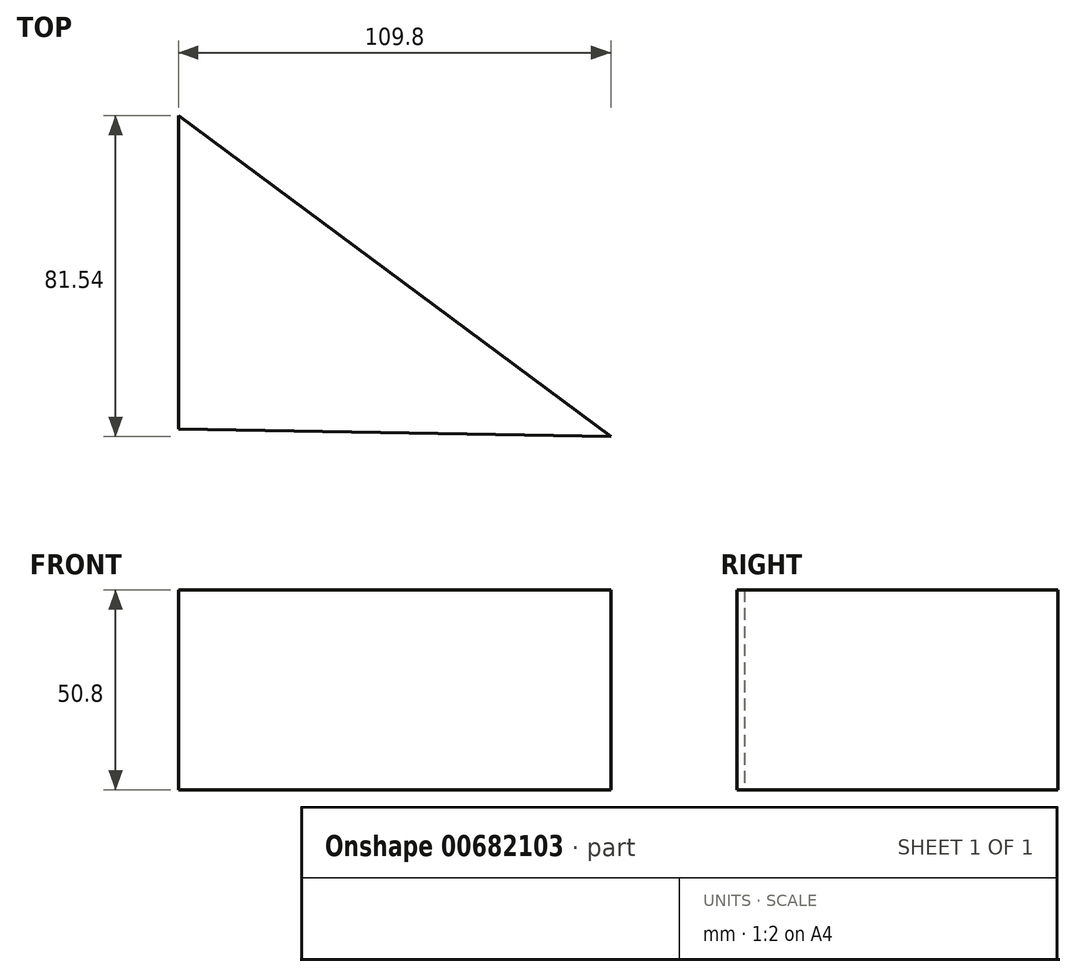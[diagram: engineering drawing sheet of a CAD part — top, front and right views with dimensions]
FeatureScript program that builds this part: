
annotation { "Feature Type Name" : "Feature", "Feature Type Description" : "" }
export const myFeature = defineFeature(function(context is Context, id is Id, definition is map)
    precondition{}
    {
        {
            var Q0;
            Q0=qCreatedBy(makeId("Top.planeOp"),FACE);
            var sketch = newSketch(context, id + "F0", { "sketchPlane" : qUnion([Q0])});
            skLineSegment(sketch, "E0", {"start": v(-58.34, 39.24) * mm, "end": v(-58.34, -40.39) * mm});
            skLineSegment(sketch, "E1", {"start": v(-58.34, -40.39) * mm, "end": v(51.46, -42.3) * mm});
            skLineSegment(sketch, "E2", {"start": v(51.46, -42.3) * mm, "end": v(-58.34, 39.24) * mm});
            skSolve(sketch);
        }
        {
            var Q0;
            Q0 = qSketchRegion(id + "F0", true);
            extrude(context, id + "F1", {"entities" : qUnion([Q0]), "depth" : 50.8 * mm, "offsetDistance" : 25.4 * mm});
        }
    });
